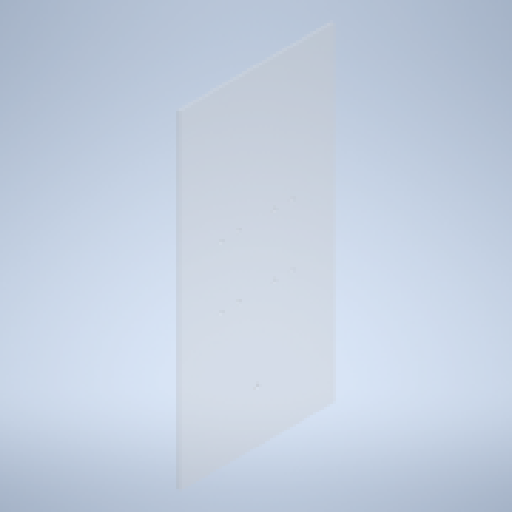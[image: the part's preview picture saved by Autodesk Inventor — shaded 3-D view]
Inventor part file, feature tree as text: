
AUTODESK INVENTOR PART (.ipt)
format: ipt  version: 2024 (Build 280153000, 153)  size: 163,840 bytes
history: native  units: mm
features: sketch x2, other x1, extrude x1, hole x1
ambient origin geometry x8: Origin, YZ Plane, XZ Plane, XY Plane, X Axis, Y Axis, Z Axis, Center Point
bodies: Body1 (feature_tree)
feature tree (5):
  other  "솔리드1"
  extrude  "돌출1"  Depth=320.0mm
  hole  "구멍1"  [1 undecoded]
  sketch  "스케치1"
  sketch  "스케치2"
note: 1 required parameter value undecoded (feature->parameter linkage not recoverable at this tier; creation-order binding heuristic only, values carry confidence <= 0.55)
